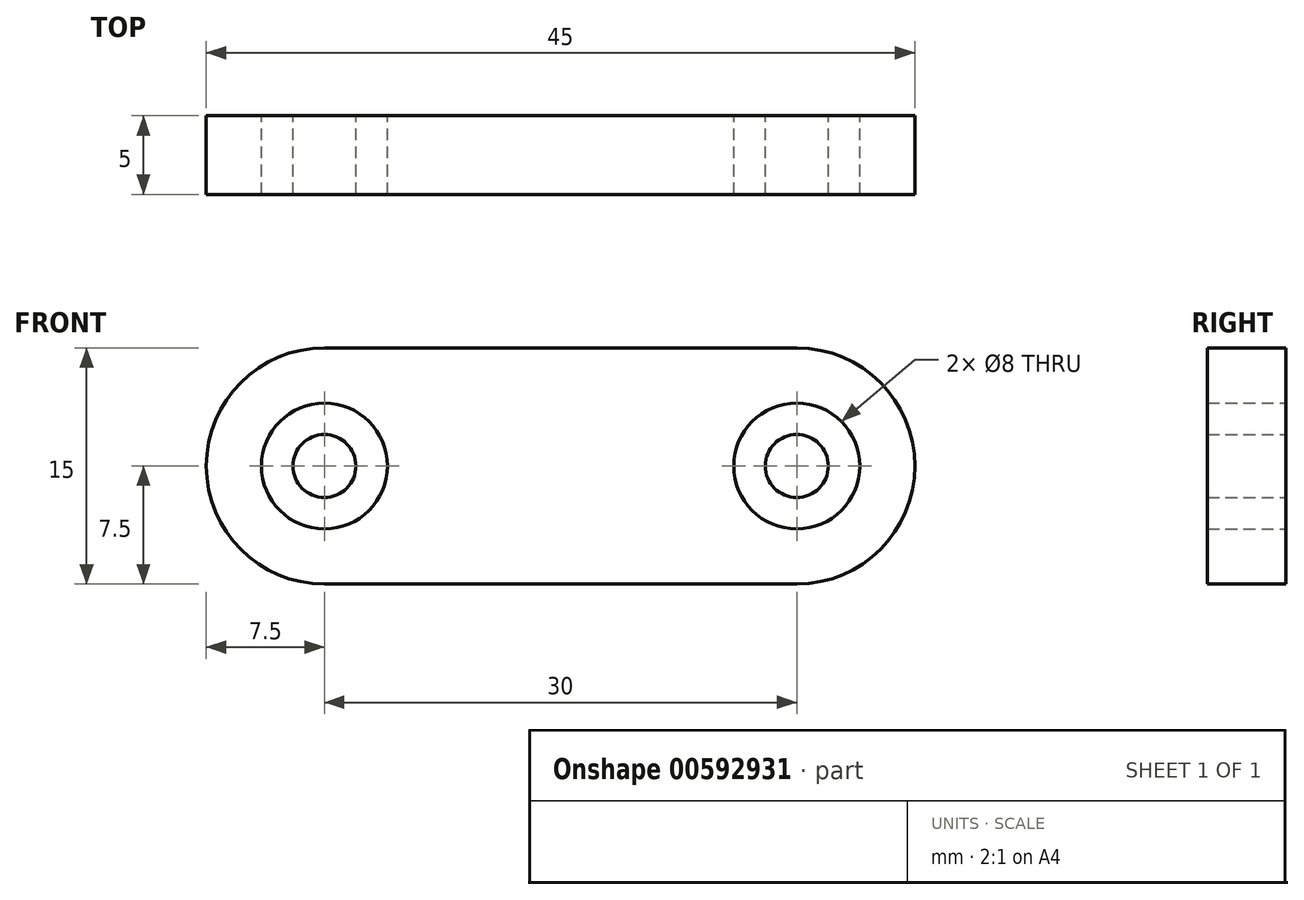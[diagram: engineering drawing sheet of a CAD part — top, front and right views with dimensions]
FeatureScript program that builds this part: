
annotation { "Feature Type Name" : "Feature", "Feature Type Description" : "" }
export const myFeature = defineFeature(function(context is Context, id is Id, definition is map)
    precondition{}
    {
        {
            var Q0;
            Q0=qCreatedBy(makeId("Front.planeOp"),FACE);
            var sketch = newSketch(context, id + "F0", { "sketchPlane" : qUnion([Q0])});
            skArc(sketch, "E0", {"start": v(0, 7.5) * mm, "mid": v(-7.5, 0) * mm, "end": v(0, -7.5) * mm});
            skArc(sketch, "E1", {"start": v(30, -7.5) * mm, "mid": v(37.5, 0) * mm, "end": v(30, 7.5) * mm});
            skLineSegment(sketch, "E2", {"start": v(0, 7.5) * mm, "end": v(30, 7.5) * mm});
            skLineSegment(sketch, "E3", {"start": v(0, -7.5) * mm, "end": v(30, -7.5) * mm});
            skCircle(sketch, "E4", {"center": v(0, 0) * mm, "radius": 4 * mm});
            skCircle(sketch, "E5", {"center": v(30, 0) * mm, "radius": 4 * mm});
            skCircle(sketch, "E6", {"center": v(0, 0) * mm, "radius": 2 * mm});
            skCircle(sketch, "E7", {"center": v(30, 0) * mm, "radius": 2 * mm});
            skSolve(sketch);
        }
        {
            var Q0;
            Q0=makeQuery(id+"F0.imprint","IMPRINT",FACE,{"disambiguationData":[TD([[makeQuery(id+"F0.imprint","IMPRINT",EDGE,{"derivedFrom":sQuery(id+"F0.wireOp",EDGE,"E0")}),1.0]])]});
            var Q1;
            Q1=makeQuery(id+"F0.imprint","IMPRINT",FACE,{"disambiguationData":[TD([[makeQuery(id+"F0.imprint","IMPRINT",EDGE,{"derivedFrom":sQuery(id+"F0.wireOp",EDGE,"E6")}),1.0]])]});
            var Q2;
            Q2=makeQuery(id+"F0.imprint","IMPRINT",FACE,{"disambiguationData":[TD([[makeQuery(id+"F0.imprint","IMPRINT",EDGE,{"derivedFrom":sQuery(id+"F0.wireOp",EDGE,"E7")}),1.0]])]});
            extrude(context, id + "F1", {"entities" : qUnion([Q0, Q1, Q2]), "depth" : 5 * mm, "offsetDistance" : 25 * mm});
        }
    });
